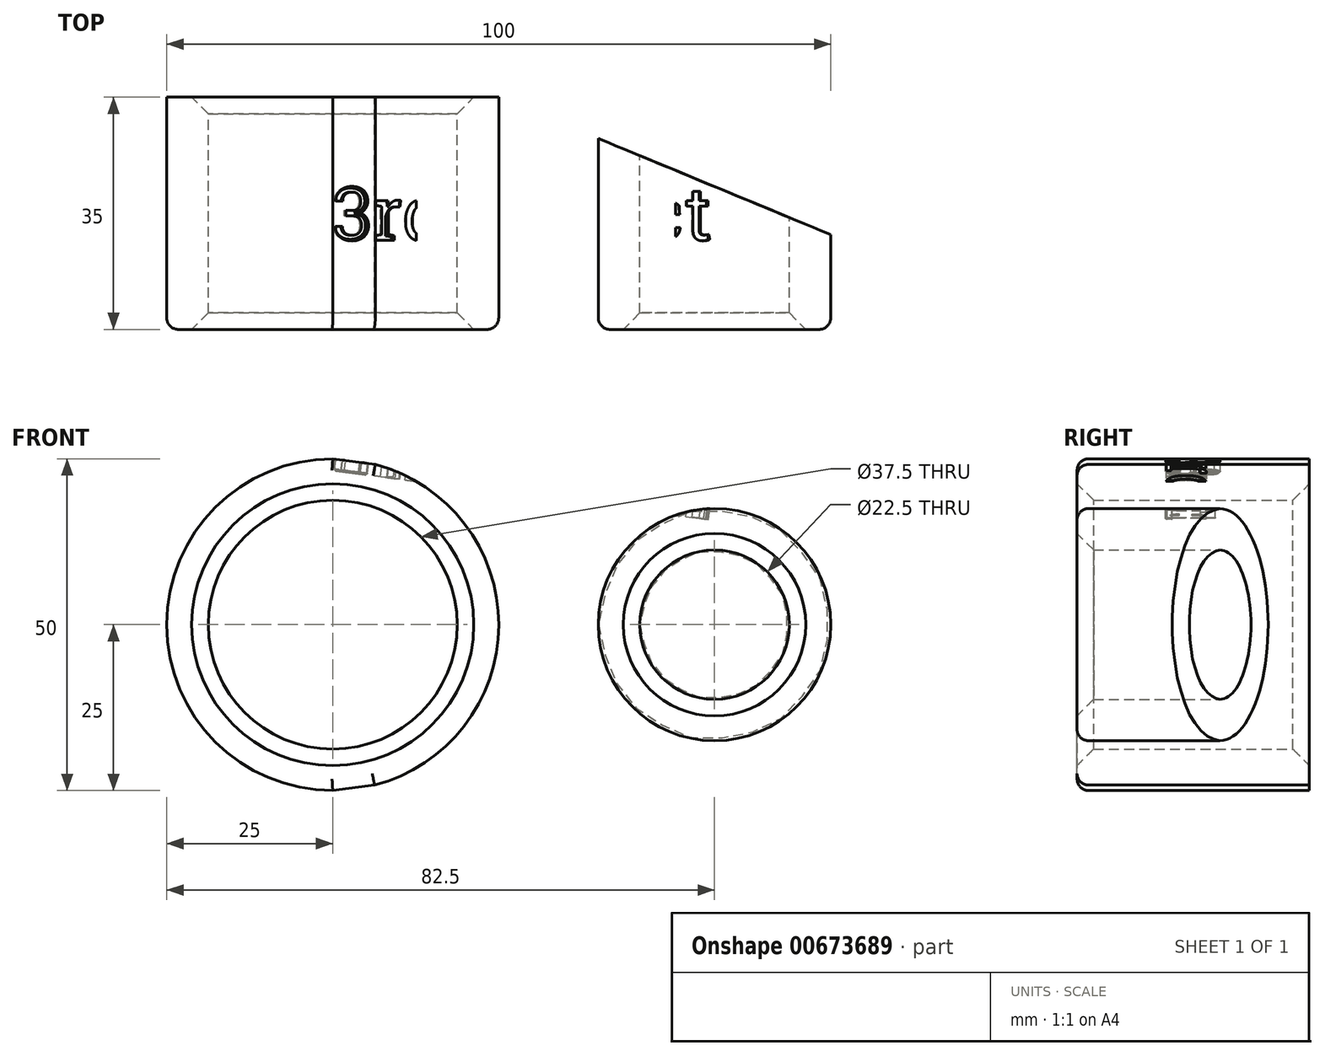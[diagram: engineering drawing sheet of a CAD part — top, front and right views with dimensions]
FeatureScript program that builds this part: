
annotation { "Feature Type Name" : "Feature", "Feature Type Description" : "" }
export const myFeature = defineFeature(function(context is Context, id is Id, definition is map)
    precondition{}
    {
        {
            var Q0;
            Q0=qCreatedBy(makeId("Front.planeOp"),FACE);
            var sketch = newSketch(context, id + "F0", { "sketchPlane" : qUnion([Q0])});
            skCircle(sketch, "E0", {"center": v(0, 0) * mm, "radius": 25 * mm});
            skCircle(sketch, "E1", {"center": v(57.5, 0) * mm, "radius": 17.5 * mm});
            skLineSegment(sketch, "E2", {"start": v(0, 25) * mm, "end": v(57.5, 17.5) * mm});
            skLineSegment(sketch, "E3", {"start": v(0, -25) * mm, "end": v(59.72, -17.36) * mm});
            skCircle(sketch, "E4", {"center": v(0, 0) * mm, "radius": 18.75 * mm});
            skCircle(sketch, "E5", {"center": v(57.5, 0) * mm, "radius": 11.25 * mm});
            skSolve(sketch);
        }
        {
            var Q0;
            {var subQ0=sQuery(id+"F0.wireOp",EDGE,"E2");var subQ1=sQuery(id+"F0.wireOp",EDGE,"E0");var subQ2=makeQuery(id+"F0.imprint","INTERSECT",VERTEX,{"disambiguationData":[OD(1.0)],"derivedFrom":[subQ1,subQ0]});Q0=makeQuery(id+"F0.imprint","IMPRINT",FACE,{"disambiguationData":[TD([[makeQuery(id+"F0.imprint","IMPRINT",EDGE,{"disambiguationData":[TD([[subQ2,1.0]])],"derivedFrom":subQ1}),-1.0]])]});}
            var Q1;
            Q1=makeQuery(id+"F0.imprint","IMPRINT",FACE,{"disambiguationData":[TD([[makeQuery(id+"F0.imprint","IMPRINT",EDGE,{"derivedFrom":sQuery(id+"F0.wireOp",EDGE,"E4")}),-1.0]])]});
            var Q2;
            Q2=makeQuery(id+"F0.imprint","IMPRINT",FACE,{"disambiguationData":[TD([[makeQuery(id+"F0.imprint","IMPRINT",EDGE,{"derivedFrom":sQuery(id+"F0.wireOp",EDGE,"E5")}),-1.0]])]});
            extrude(context, id + "F1", {"entities" : qUnion([Q0, Q1, Q2]), "depth" : 17.5 * mm, "offsetDistance" : 25 * mm, "hasSecondDirection" : true, "secondDirectionOppositeDirection" : true, "secondDirectionDepth" : 17.5 * mm});
        }
        {
            var Q0;
            Q0=qCreatedBy(makeId("Top.planeOp"),FACE);
            var sketch = newSketch(context, id + "F2", { "sketchPlane" : qUnion([Q0])});
            skPoint(sketch, "E6", {"position": v(0, 17.5) * mm});
            skLineSegment(sketch, "E7", {"start": v(25, 17.5) * mm, "end": v(75, 17.5) * mm});
            skLineSegment(sketch, "E8", {"start": v(25, 17.5) * mm, "end": v(75, -3.21) * mm});
            skLineSegment(sketch, "E9", {"start": v(75, -3.21) * mm, "end": v(75, 17.5) * mm});
            skLineSegment(sketch, "E10", {"start": v(75, 17.5) * mm, "end": v(75, -17.5) * mm});
            skSolve(sketch);
        }
        {
            var Q0;
            Q0 = qSketchRegion(id + "F2", true);
            extrude(context, id + "F3", {"entities" : qUnion([Q0]), "operationType" : NewBodyOperationType.REMOVE, "oppositeDirection" : true, "depth" : 25 * mm, "offsetDistance" : 25 * mm, "hasSecondDirection" : true, "secondDirectionOppositeDirection" : false, "secondDirectionDepth" : 25 * mm});
        }
        {
            var Q0;
            Q0=makeQuery(id+"F1.opExtrude","SWEPT_FACE",FACE,{"disambiguationData":[OSD([sQuery(id+"F0.wireOp",EDGE,"E2")])]});
            var sketch = newSketch(context, id + "F4", { "sketchPlane" : qUnion([Q0])});
            skPoint(sketch, "E11", {"position": v(54.75, 0) * mm});
            skPoint(sketch, "E12", {"position": v(54.75, -4.04) * mm});
            skPoint(sketch, "E13", {"position": v(-3.23, 4.04) * mm});
            skText(sketch, "E14", { "text": "3rd Project", "fontName": "RobotoSlab-Regular.ttf"});
            const initialGuessF4  = {"E14": [-0.00323, -0.00404, 1, 0, 0.00808]};
            skSetInitialGuess(sketch, initialGuessF4);
            skSolve(sketch);
        }
        {
            var Q0;
            Q0=makeQuery(id+"F4.imprint","IMPRINT",FACE,{"disambiguationData":[TD([[makeQuery(id+"F4.imprint","IMPRINT",EDGE,{"derivedFrom":sQuery(id+"F4.wireOp",EDGE,"E14.sketch_text.stroke-0")}),-1.0]])]});
            var Q1;
            Q1=makeQuery(id+"F4.imprint","IMPRINT",FACE,{"disambiguationData":[TD([[makeQuery(id+"F4.imprint","IMPRINT",EDGE,{"derivedFrom":sQuery(id+"F4.wireOp",EDGE,"E14.sketch_text.stroke-50")}),-1.0]])]});
            var Q2;
            Q2=makeQuery(id+"F4.imprint","IMPRINT",FACE,{"disambiguationData":[TD([[makeQuery(id+"F4.imprint","IMPRINT",EDGE,{"derivedFrom":sQuery(id+"F4.wireOp",EDGE,"E14.sketch_text.stroke-102")}),-1.0]])]});
            var Q3;
            Q3=makeQuery(id+"F4.imprint","IMPRINT",FACE,{"disambiguationData":[TD([[makeQuery(id+"F4.imprint","IMPRINT",EDGE,{"derivedFrom":sQuery(id+"F4.wireOp",EDGE,"E14.sketch_text.stroke-206")}),-1.0]])]});
            var Q4;
            Q4=makeQuery(id+"F4.imprint","IMPRINT",FACE,{"disambiguationData":[TD([[makeQuery(id+"F4.imprint","IMPRINT",EDGE,{"derivedFrom":sQuery(id+"F4.wireOp",EDGE,"E14.sketch_text.stroke-121")}),-1.0]])]});
            var Q5;
            Q5=makeQuery(id+"F4.imprint","IMPRINT",FACE,{"disambiguationData":[TD([[makeQuery(id+"F4.imprint","IMPRINT",EDGE,{"derivedFrom":sQuery(id+"F4.wireOp",EDGE,"E14.sketch_text.stroke-183")}),-1.0]])]});
            var Q6;
            Q6=makeQuery(id+"F4.imprint","IMPRINT",FACE,{"disambiguationData":[TD([[makeQuery(id+"F4.imprint","IMPRINT",EDGE,{"derivedFrom":sQuery(id+"F4.wireOp",EDGE,"E14.sketch_text.stroke-141")}),-1.0]])]});
            var Q7;
            Q7=makeQuery(id+"F4.imprint","IMPRINT",FACE,{"disambiguationData":[TD([[makeQuery(id+"F4.imprint","IMPRINT",EDGE,{"derivedFrom":sQuery(id+"F4.wireOp",EDGE,"E14.sketch_text.stroke-79")}),-1.0]])]});
            var Q8;
            Q8=makeQuery(id+"F4.imprint","IMPRINT",FACE,{"disambiguationData":[TD([[makeQuery(id+"F4.imprint","IMPRINT",EDGE,{"derivedFrom":sQuery(id+"F4.wireOp",EDGE,"E14.sketch_text.stroke-159")}),-1.0]])]});
            var Q9;
            Q9=makeQuery(id+"F4.imprint","IMPRINT",FACE,{"disambiguationData":[TD([[makeQuery(id+"F4.imprint","IMPRINT",EDGE,{"derivedFrom":sQuery(id+"F4.wireOp",EDGE,"E14.sketch_text.stroke-31")}),-1.0]])]});
            var Q10;
            Q10=makeQuery(id+"F4.imprint","IMPRINT",FACE,{"disambiguationData":[TD([[makeQuery(id+"F4.imprint","IMPRINT",EDGE,{"derivedFrom":sQuery(id+"F4.wireOp",EDGE,"E14.sketch_text.stroke-155")}),-1.0]])]});
            extrude(context, id + "F5", {"entities" : qUnion([Q0, Q1, Q2, Q3, Q4, Q5, Q6, Q7, Q8, Q9, Q10]), "operationType" : NewBodyOperationType.REMOVE, "oppositeDirection" : true, "depth" : 1.75 * mm, "offsetDistance" : 25 * mm});
        }
        {
            var Q0;
            Q0=makeQuery(id+"F1.opExtrude","CAP_EDGE",EDGE,{"disambiguationData":[OSD([sQuery(id+"F0.wireOp",EDGE,"E2")])],"isStart":false});
            var Q1;
            Q1=makeQuery(id+"F1.opExtrude","CAP_EDGE",EDGE,{"disambiguationData":[OSD([sQuery(id+"F0.wireOp",EDGE,"E3")])],"isStart":false});
            var Q2;
            Q2=makeQuery(id+"F1.opExtrude","CAP_EDGE",EDGE,{"disambiguationData":[OSD([sQuery(id+"F0.wireOp",EDGE,"E0")])],"isStart":false});
            var Q3;
            Q3=makeQuery(id+"F1.opExtrude","CAP_EDGE",EDGE,{"disambiguationData":[OSD([sQuery(id+"F0.wireOp",EDGE,"E1")])],"isStart":false});
            fillet(context, id + "F6", {"entities" : qUnion([Q0, Q1, Q2, Q3]), "radius" : 1.75 * mm, "tangentPropagation" : true, "allowEdgeOverflow" : false});
        }
        {
            var Q0;
            Q0=makeQuery(id+"F1.opExtrude","CAP_EDGE",EDGE,{"disambiguationData":[OSD([sQuery(id+"F0.wireOp",EDGE,"E4")])],"isStart":true});
            var Q1;
            Q1=makeQuery(id+"F1.opExtrude","CAP_EDGE",EDGE,{"disambiguationData":[OSD([sQuery(id+"F0.wireOp",EDGE,"E5")])],"isStart":false});
            var Q2;
            Q2=makeQuery(id+"F1.opExtrude","CAP_EDGE",EDGE,{"disambiguationData":[OSD([sQuery(id+"F0.wireOp",EDGE,"E4")])],"isStart":false});
            chamfer(context, id + "F7", {"entities" : qUnion([Q0, Q1, Q2]), "width" : 2.5 * mm, "tangentPropagation" : true});
        }
        {
            var Q0;
            Q0=makeQuery(id+"F5.boolean.opBoolean","COPY",EDGE,{"derivedFrom":makeQuery(id+"F5.opExtrude","CAP_EDGE",EDGE,{"disambiguationData":[OSD([sQuery(id+"F4.wireOp",EDGE,"E14.sketch_text.stroke-64")])],"isStart":true})});
            var Q1;
            Q1=makeQuery(id+"F5.boolean.opBoolean","COPY",EDGE,{"derivedFrom":makeQuery(id+"F5.opExtrude","CAP_EDGE",EDGE,{"disambiguationData":[OSD([sQuery(id+"F4.wireOp",EDGE,"E14.sketch_text.stroke-59")])],"isStart":true})});
            var Q2;
            Q2=makeQuery(id+"F5.boolean.opBoolean","COPY",EDGE,{"derivedFrom":makeQuery(id+"F5.opExtrude","CAP_EDGE",EDGE,{"disambiguationData":[OSD([sQuery(id+"F4.wireOp",EDGE,"E14.sketch_text.stroke-61")])],"isStart":true})});
            var Q3;
            Q3=makeQuery(id+"F5.boolean.opBoolean","COPY",EDGE,{"derivedFrom":makeQuery(id+"F5.opExtrude","CAP_EDGE",EDGE,{"disambiguationData":[OSD([sQuery(id+"F4.wireOp",EDGE,"E14.sketch_text.stroke-62"),sQuery(id+"F4.wireOp",EDGE,"E14.sketch_text.stroke-63")])],"isStart":true})});
            var Q4;
            Q4=makeQuery(id+"F5.boolean.opBoolean","COPY",EDGE,{"derivedFrom":makeQuery(id+"F5.opExtrude","CAP_EDGE",EDGE,{"disambiguationData":[OSD([sQuery(id+"F4.wireOp",EDGE,"E14.sketch_text.stroke-73")])],"isStart":true})});
            var Q5;
            Q5=makeQuery(id+"F5.boolean.opBoolean","COPY",EDGE,{"derivedFrom":makeQuery(id+"F5.opExtrude","CAP_EDGE",EDGE,{"disambiguationData":[OSD([sQuery(id+"F4.wireOp",EDGE,"E14.sketch_text.stroke-75")])],"isStart":true})});
            var Q6;
            Q6=makeQuery(id+"F5.boolean.opBoolean","COPY",EDGE,{"derivedFrom":makeQuery(id+"F5.opExtrude","CAP_EDGE",EDGE,{"disambiguationData":[OSD([sQuery(id+"F4.wireOp",EDGE,"E14.sketch_text.stroke-74")])],"isStart":true})});
            var Q7;
            Q7=makeQuery(id+"F5.boolean.opBoolean","COPY",EDGE,{"derivedFrom":makeQuery(id+"F5.opExtrude","CAP_EDGE",EDGE,{"disambiguationData":[OSD([sQuery(id+"F4.wireOp",EDGE,"E14.sketch_text.stroke-56")])],"isStart":true})});
            var Q8;
            Q8=makeQuery(id+"F5.boolean.opBoolean","COPY",EDGE,{"derivedFrom":makeQuery(id+"F5.opExtrude","CAP_EDGE",EDGE,{"disambiguationData":[OSD([sQuery(id+"F4.wireOp",EDGE,"E14.sketch_text.stroke-40")])],"isStart":true})});
            var Q9;
            Q9=makeQuery(id+"F5.boolean.opBoolean","COPY",EDGE,{"derivedFrom":makeQuery(id+"F5.opExtrude","CAP_EDGE",EDGE,{"disambiguationData":[OSD([sQuery(id+"F4.wireOp",EDGE,"E14.sketch_text.stroke-38")])],"isStart":true})});
            var Q10;
            Q10=makeQuery(id+"F5.boolean.opBoolean","COPY",EDGE,{"derivedFrom":makeQuery(id+"F5.opExtrude","CAP_EDGE",EDGE,{"disambiguationData":[OSD([sQuery(id+"F4.wireOp",EDGE,"E14.sketch_text.stroke-48")])],"isStart":true})});
            var Q11;
            Q11=makeQuery(id+"F5.boolean.opBoolean","COPY",EDGE,{"derivedFrom":makeQuery(id+"F5.opExtrude","CAP_EDGE",EDGE,{"disambiguationData":[OSD([sQuery(id+"F4.wireOp",EDGE,"E14.sketch_text.stroke-49")])],"isStart":true})});
            var Q12;
            Q12=makeQuery(id+"F5.boolean.opBoolean","COPY",EDGE,{"derivedFrom":makeQuery(id+"F5.opExtrude","CAP_EDGE",EDGE,{"disambiguationData":[OSD([sQuery(id+"F4.wireOp",EDGE,"E14.sketch_text.stroke-31")])],"isStart":true})});
            var Q13;
            Q13=makeQuery(id+"F5.boolean.opBoolean","COPY",EDGE,{"derivedFrom":makeQuery(id+"F5.opExtrude","CAP_EDGE",EDGE,{"disambiguationData":[OSD([sQuery(id+"F4.wireOp",EDGE,"E14.sketch_text.stroke-32")])],"isStart":true})});
            var Q14;
            Q14=makeQuery(id+"F5.boolean.opBoolean","COPY",EDGE,{"derivedFrom":makeQuery(id+"F5.opExtrude","CAP_EDGE",EDGE,{"disambiguationData":[OSD([sQuery(id+"F4.wireOp",EDGE,"E14.sketch_text.stroke-33")])],"isStart":true})});
            var Q15;
            Q15=makeQuery(id+"F5.boolean.opBoolean","COPY",EDGE,{"derivedFrom":makeQuery(id+"F5.opExtrude","CAP_EDGE",EDGE,{"disambiguationData":[OSD([sQuery(id+"F4.wireOp",EDGE,"E14.sketch_text.stroke-42")])],"isStart":false})});
            var Q16;
            Q16=makeQuery(id+"F5.boolean.opBoolean","COPY",EDGE,{"derivedFrom":makeQuery(id+"F5.opExtrude","CAP_EDGE",EDGE,{"disambiguationData":[OSD([sQuery(id+"F4.wireOp",EDGE,"E14.sketch_text.stroke-44")])],"isStart":false})});
            var Q17;
            Q17=makeQuery(id+"F5.boolean.opBoolean","COPY",EDGE,{"derivedFrom":makeQuery(id+"F5.opExtrude","CAP_EDGE",EDGE,{"disambiguationData":[OSD([sQuery(id+"F4.wireOp",EDGE,"E14.sketch_text.stroke-43")])],"isStart":false})});
            var Q18;
            Q18=makeQuery(id+"F5.boolean.opBoolean","COPY",EDGE,{"derivedFrom":makeQuery(id+"F5.opExtrude","CAP_EDGE",EDGE,{"disambiguationData":[OSD([sQuery(id+"F4.wireOp",EDGE,"E14.sketch_text.stroke-47")])],"isStart":true})});
            var Q19;
            Q19=makeQuery(id+"F5.boolean.opBoolean","COPY",EDGE,{"derivedFrom":makeQuery(id+"F5.opExtrude","CAP_EDGE",EDGE,{"disambiguationData":[OSD([sQuery(id+"F4.wireOp",EDGE,"E14.sketch_text.stroke-46")])],"isStart":true})});
            var Q20;
            Q20=makeQuery(id+"F5.boolean.opBoolean","COPY",EDGE,{"derivedFrom":makeQuery(id+"F5.opExtrude","CAP_EDGE",EDGE,{"disambiguationData":[OSD([sQuery(id+"F4.wireOp",EDGE,"E14.sketch_text.stroke-45")])],"isStart":true})});
            var Q21;
            Q21=makeQuery(id+"F5.boolean.opBoolean","COPY",EDGE,{"derivedFrom":makeQuery(id+"F5.opExtrude","CAP_EDGE",EDGE,{"disambiguationData":[OSD([sQuery(id+"F4.wireOp",EDGE,"E14.sketch_text.stroke-35")])],"isStart":true})});
            var Q22;
            Q22=makeQuery(id+"F5.boolean.opBoolean","COPY",EDGE,{"derivedFrom":makeQuery(id+"F5.opExtrude","CAP_EDGE",EDGE,{"disambiguationData":[OSD([sQuery(id+"F4.wireOp",EDGE,"E14.sketch_text.stroke-16")])],"isStart":false})});
            var Q23;
            Q23=makeQuery(id+"F5.boolean.opBoolean","COPY",EDGE,{"derivedFrom":makeQuery(id+"F5.opExtrude","CAP_EDGE",EDGE,{"disambiguationData":[OSD([sQuery(id+"F4.wireOp",EDGE,"E14.sketch_text.stroke-26")])],"isStart":true})});
            var Q24;
            Q24=makeQuery(id+"F5.boolean.opBoolean","COPY",EDGE,{"derivedFrom":makeQuery(id+"F5.opExtrude","CAP_EDGE",EDGE,{"disambiguationData":[OSD([sQuery(id+"F4.wireOp",EDGE,"E14.sketch_text.stroke-22")])],"isStart":true})});
            var Q25;
            Q25=makeQuery(id+"F5.boolean.opBoolean","COPY",EDGE,{"derivedFrom":makeQuery(id+"F5.opExtrude","CAP_EDGE",EDGE,{"disambiguationData":[OSD([sQuery(id+"F4.wireOp",EDGE,"E14.sketch_text.stroke-30")])],"isStart":true})});
            var Q26;
            Q26=makeQuery(id+"F5.boolean.opBoolean","COPY",EDGE,{"derivedFrom":makeQuery(id+"F5.opExtrude","CAP_EDGE",EDGE,{"disambiguationData":[OSD([sQuery(id+"F4.wireOp",EDGE,"E14.sketch_text.stroke-2")])],"isStart":true})});
            var Q27;
            Q27=makeQuery(id+"F5.boolean.opBoolean","COPY",EDGE,{"derivedFrom":makeQuery(id+"F5.opExtrude","CAP_EDGE",EDGE,{"disambiguationData":[OSD([sQuery(id+"F4.wireOp",EDGE,"E14.sketch_text.stroke-13")])],"isStart":false})});
            var Q28;
            Q28=makeQuery(id+"F5.boolean.opBoolean","COPY",EDGE,{"derivedFrom":makeQuery(id+"F5.opExtrude","CAP_EDGE",EDGE,{"disambiguationData":[OSD([sQuery(id+"F4.wireOp",EDGE,"E14.sketch_text.stroke-7")])],"isStart":true})});
            chamfer(context, id + "F8", {"entities" : qUnion([Q0, Q1, Q2, Q3, Q4, Q5, Q6, Q7, Q8, Q9, Q10, Q11, Q12, Q13, Q14, Q15, Q16, Q17, Q18, Q19, Q20, Q21, Q22, Q23, Q24, Q25, Q26, Q27, Q28]), "width" : 0.25 * mm, "tangentPropagation" : true});
        }
    });
